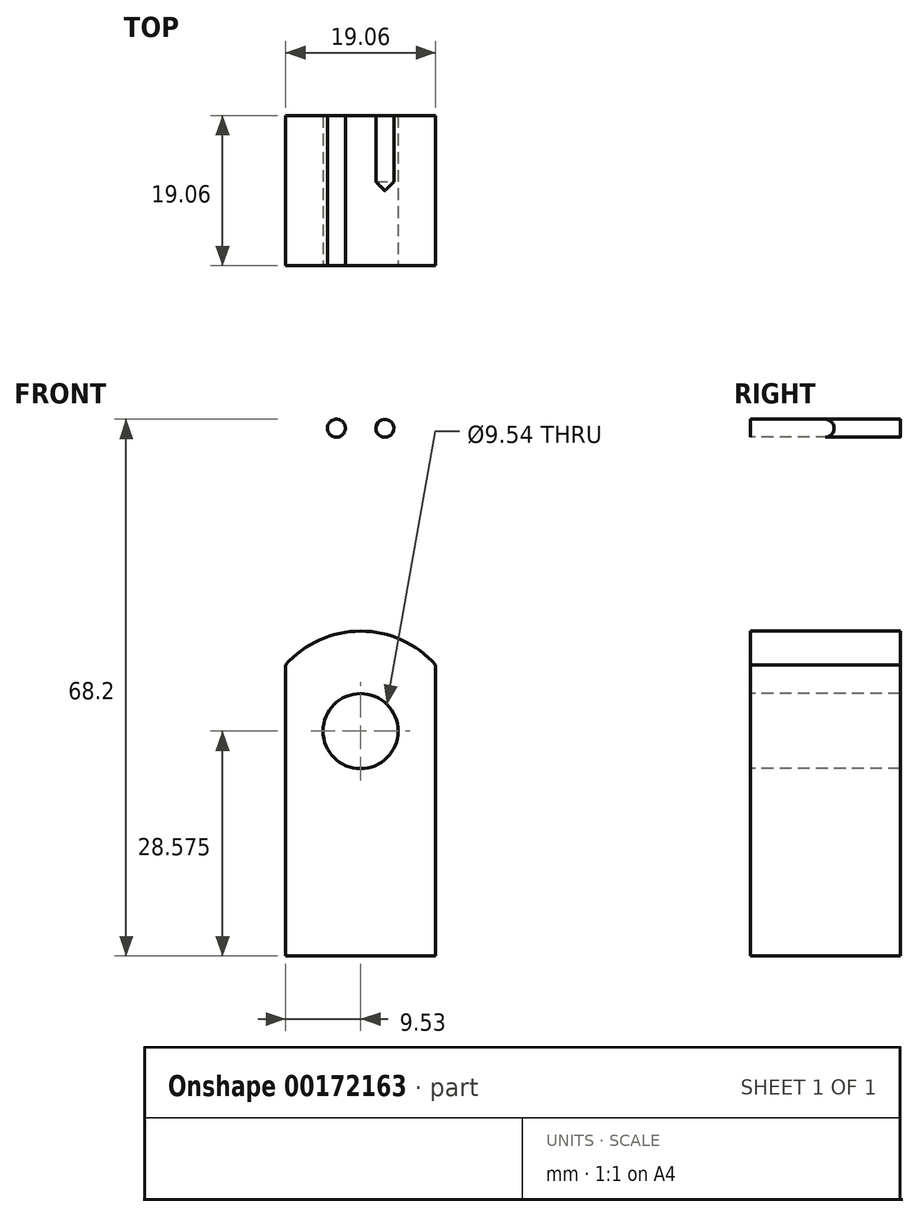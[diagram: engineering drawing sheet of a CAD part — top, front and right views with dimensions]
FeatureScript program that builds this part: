
annotation { "Feature Type Name" : "Feature", "Feature Type Description" : "" }
export const myFeature = defineFeature(function(context is Context, id is Id, definition is map)
    precondition{}
    {
        {
            var Q0;
            Q0=qCreatedBy(makeId("Top.planeOp"),FACE);
            var sketch = newSketch(context, id + "F0", { "sketchPlane" : qUnion([Q0])});
            skLineSegment(sketch, "E0.bottom", {"start": v(9.53, 9.53) * mm, "end": v(-9.52, 9.53) * mm});
            skLineSegment(sketch, "E0.top", {"start": v(9.53, -9.52) * mm, "end": v(-9.53, -9.52) * mm});
            skLineSegment(sketch, "E0.left", {"start": v(9.53, 9.53) * mm, "end": v(9.53, -9.52) * mm});
            skLineSegment(sketch, "E0.right", {"start": v(-9.52, 9.53) * mm, "end": v(-9.53, -9.52) * mm});
            skPoint(sketch, "E0.middle", {"position": v(0, 0) * mm});
            skSolve(sketch);
        }
        {
            var Q0;
            Q0=makeQuery(id+"F0.imprint","IMPRINT",FACE,{"disambiguationData":[TD([[makeQuery(id+"F0.imprint","IMPRINT",EDGE,{"derivedFrom":sQuery(id+"F0.wireOp",EDGE,"E0.bottom")}),1.0]])]});
            extrude(context, id + "F1", {"entities" : qUnion([Q0]), "oppositeDirection" : true, "depth" : 88.9 * mm});
        }
        {
            var Q0;
            Q0=makeQuery(id+"F1.opExtrude","CAP_EDGE",EDGE,{"disambiguationData":[OSD([sQuery(id+"F0.wireOp",EDGE,"E0.right")])],"isStart":true});
            var Q1;
            Q1=makeQuery(id+"F1.opExtrude","CAP_EDGE",EDGE,{"disambiguationData":[OSD([sQuery(id+"F0.wireOp",EDGE,"E0.left")])],"isStart":true});
            fillet(context, id + "F2", {"entities" : qUnion([Q0, Q1]), "radius" : 9.52 * mm, "allowEdgeOverflow" : false});
        }
        {
            var Q0;
            Q0=makeQuery(id+"F1.opExtrude","SWEPT_FACE",FACE,{"disambiguationData":[OSD([sQuery(id+"F0.wireOp",EDGE,"E0.top")])]});
            var sketch = newSketch(context, id + "F3", { "sketchPlane" : qUnion([Q0])});
            skLineSegment(sketch, "E1", {"start": v(-9.53, -9.53) * mm, "end": v(9.53, -9.53) * mm, "construction": true});
            skCircle(sketch, "E2", {"center": v(0, -9.53) * mm, "radius": 4.76 * mm});
            skCircle(sketch, "E3", {"center": v(3.08, -21.85) * mm, "radius": 1.14 * mm});
            skCircle(sketch, "E4", {"center": v(0, -60.33) * mm, "radius": 4.77 * mm});
            skCircle(sketch, "E5", {"center": v(0, -60.33) * mm, "radius": 12.7 * mm});
            skLineSegment(sketch, "E6", {"start": v(0, -9.53) * mm, "end": v(12.7, -60.33) * mm, "construction": true});
            skCircle(sketch, "E7.MirrorC", {"center": v(-3.08, -21.85) * mm, "radius": 1.14 * mm});
            skLineSegment(sketch, "E8", {"start": v(0, -9.53) * mm, "end": v(0, -60.33) * mm, "construction": true});
            skSolve(sketch);
        }
        {
            var Q0;
            Q0=makeQuery(id+"F3.imprint","IMPRINT",FACE,{"disambiguationData":[TD([[makeQuery(id+"F3.imprint","IMPRINT",EDGE,{"derivedFrom":sQuery(id+"F3.wireOp",EDGE,"E4")}),1.0]])]});
            var Q1;
            Q1=makeQuery(id+"F3.imprint","IMPRINT",FACE,{"disambiguationData":[TD([[makeQuery(id+"F3.imprint","IMPRINT",EDGE,{"derivedFrom":sQuery(id+"F3.wireOp",EDGE,"E7.MirrorC")}),-1.0]])]});
            var Q2;
            Q2=makeQuery(id+"F3.imprint","IMPRINT",FACE,{"disambiguationData":[TD([[makeQuery(id+"F3.imprint","IMPRINT",EDGE,{"derivedFrom":sQuery(id+"F3.wireOp",EDGE,"E2")}),1.0]])]});
            extrude(context, id + "F4", {"entities" : qUnion([Q0, Q1, Q2]), "operationType" : NewBodyOperationType.REMOVE, "endBound" : BoundingType.THROUGH_ALL, "oppositeDirection" : true, "depth" : 25.4 * mm});
        }
        {
            var Q0;
            Q0=makeQuery(id+"F3.imprint","IMPRINT",FACE,{"disambiguationData":[TD([[makeQuery(id+"F3.imprint","IMPRINT",EDGE,{"derivedFrom":sQuery(id+"F3.wireOp",EDGE,"E3")}),1.0]])]});
            extrude(context, id + "F5", {"entities" : qUnion([Q0]), "operationType" : NewBodyOperationType.REMOVE, "oppositeDirection" : true, "depth" : 9.52 * mm});
        }
        {
            var Q0;
            Q0=makeQuery(id+"F1.opExtrude","SWEPT_FACE",FACE,{"disambiguationData":[OSD([sQuery(id+"F0.wireOp",EDGE,"E0.left")])]});
            var sketch = newSketch(context, id + "F6", { "sketchPlane" : qUnion([Q0])});
            skCircle(sketch, "E9", {"center": v(0, -21.84) * mm, "radius": 1.14 * mm});
            skSolve(sketch);
        }
        {
            var Q0;
            Q0=makeQuery(id+"F6.imprint","IMPRINT",FACE,{"disambiguationData":[TD([[makeQuery(id+"F6.imprint","IMPRINT",EDGE,{"derivedFrom":sQuery(id+"F6.wireOp",EDGE,"E9")}),1.0]])]});
            extrude(context, id + "F7", {"entities" : qUnion([Q0]), "operationType" : NewBodyOperationType.REMOVE, "oppositeDirection" : true, "depth" : 8.9 * mm});
        }
    });
